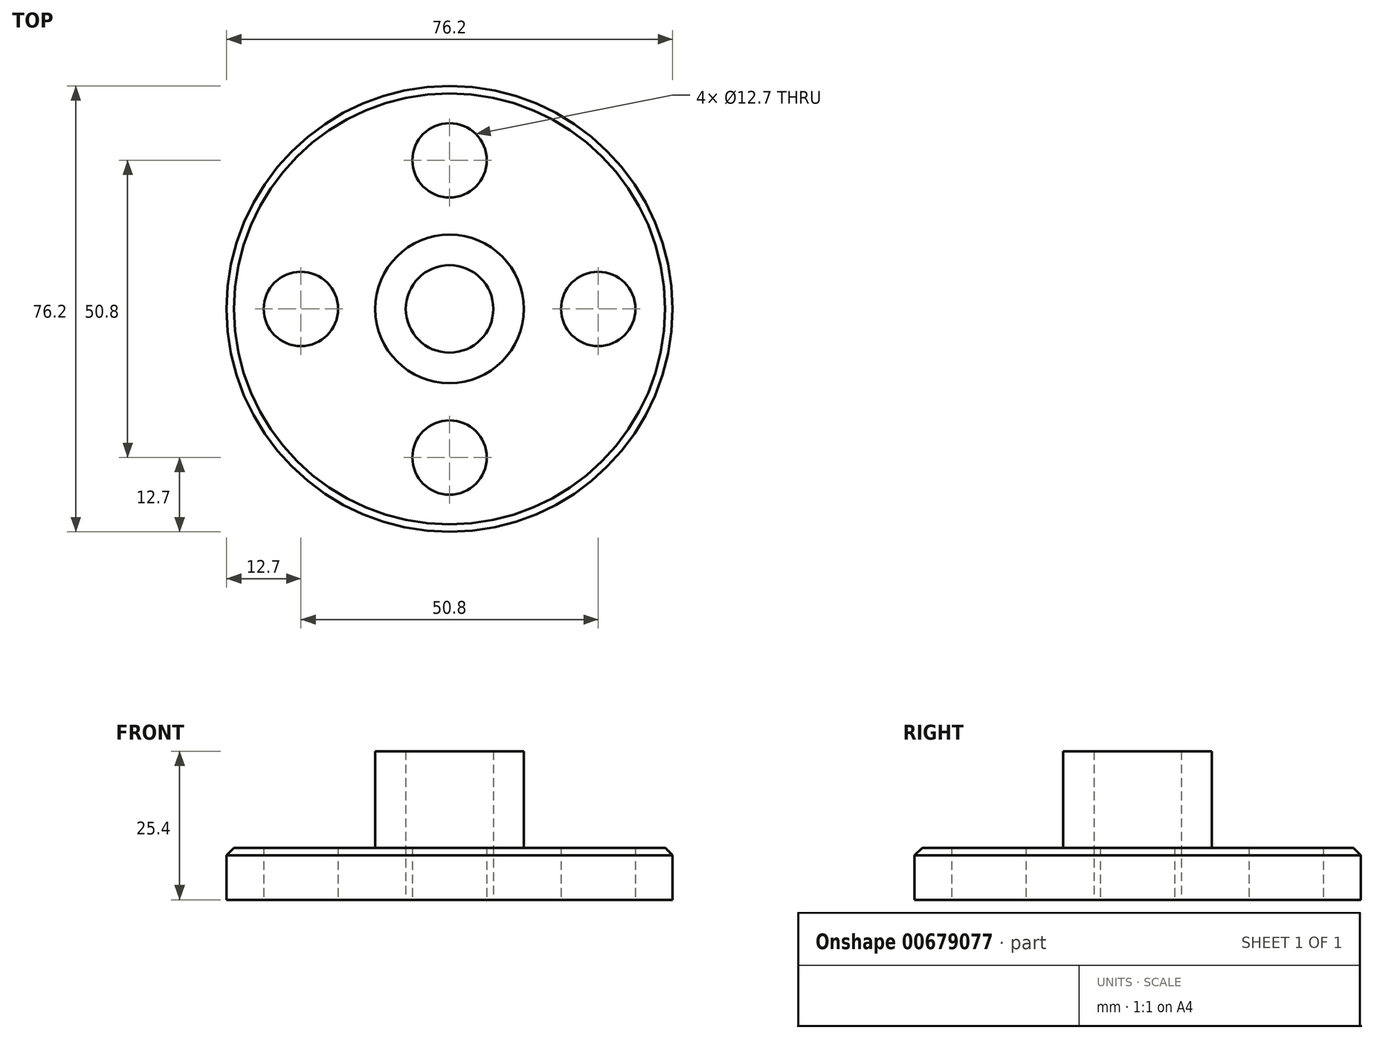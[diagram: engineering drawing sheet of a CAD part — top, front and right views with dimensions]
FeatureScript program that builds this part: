
annotation { "Feature Type Name" : "Feature", "Feature Type Description" : "" }
export const myFeature = defineFeature(function(context is Context, id is Id, definition is map)
    precondition{}
    {
        {
            var Q0;
            Q0=qCreatedBy(makeId("Top.planeOp"),FACE);
            var sketch = newSketch(context, id + "F0", { "sketchPlane" : qUnion([Q0])});
            skCircle(sketch, "E0", {"center": v(0, 0) * mm, "radius": 12.7 * mm});
            skCircle(sketch, "E1", {"center": v(0, 0) * mm, "radius": 38.1 * mm});
            skLineSegment(sketch, "E2", {"start": v(0, 12.7) * mm, "end": v(0, 38.1) * mm, "construction": true});
            skCircle(sketch, "E3", {"center": v(0, 25.4) * mm, "radius": 6.35 * mm});
            skLineSegment(sketch, "E4", {"start": v(12.7, 0) * mm, "end": v(38.1, 0) * mm, "construction": true});
            skLineSegment(sketch, "E5", {"start": v(0, -12.7) * mm, "end": v(0, -38.1) * mm, "construction": true});
            skLineSegment(sketch, "E6", {"start": v(-12.7, 0) * mm, "end": v(-38.1, 0) * mm, "construction": true});
            skCircle(sketch, "E7", {"center": v(25.4, 0) * mm, "radius": 6.35 * mm});
            skCircle(sketch, "E8", {"center": v(-25.4, 0) * mm, "radius": 6.35 * mm});
            skCircle(sketch, "E9", {"center": v(0, -25.4) * mm, "radius": 6.35 * mm});
            skSolve(sketch);
        }
        {
            var Q0;
            Q0 = qSketchRegion(id + "F0", true);
            extrude(context, id + "F1", {"entities" : qUnion([Q0]), "depth" : 8.9 * mm, "offsetDistance" : 25.4 * mm});
        }
        {
            var Q0;
            Q0=makeQuery(id+"F1.opExtrude","CAP_EDGE",EDGE,{"disambiguationData":[OSD([sQuery(id+"F0.wireOp",EDGE,"E1")])],"isStart":false});
            chamfer(context, id + "F2", {"entities" : qUnion([Q0]), "width" : 1.27 * mm, "tangentPropagation" : true});
        }
        {
            var Q0;
            Q0=makeQuery(id+"F0.imprint","IMPRINT",FACE,{"disambiguationData":[TD([[makeQuery(id+"F0.imprint","IMPRINT",EDGE,{"derivedFrom":sQuery(id+"F0.wireOp",EDGE,"E0")}),1.0]])]});
            extrude(context, id + "F3", {"entities" : qUnion([Q0]), "operationType" : NewBodyOperationType.ADD, "depth" : 25.4 * mm, "offsetDistance" : 25.4 * mm});
        }
        {
            var Q0;
            Q0=qCreatedBy(makeId("Top.planeOp"),FACE);
            var sketch = newSketch(context, id + "F4", { "sketchPlane" : qUnion([Q0])});
            skCircle(sketch, "E10", {"center": v(0, 0) * mm, "radius": 7.48 * mm});
            skSolve(sketch);
        }
        {
            var Q0;
            Q0=makeQuery(id+"F4.imprint","IMPRINT",FACE,{"disambiguationData":[TD([[makeQuery(id+"F4.imprint","IMPRINT",EDGE,{"derivedFrom":sQuery(id+"F4.wireOp",EDGE,"E10")}),1.0]])]});
            var Q1;
            Q1=sQuery(id+"F4.wireOp",EDGE,"E10");
            extrude(context, id + "F5", {"entities" : qUnion([Q0]), "operationType" : NewBodyOperationType.REMOVE, "surfaceEntities" : qUnion([Q1]), "depth" : 173.48 * mm, "offsetDistance" : 25.4 * mm});
        }
    });
